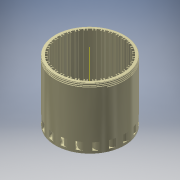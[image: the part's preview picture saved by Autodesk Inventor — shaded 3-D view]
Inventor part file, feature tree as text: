
AUTODESK INVENTOR PART (.ipt)
format: ipt  version: 2017 (Build 210142000, 142)  size: 1,598,976 bytes
history: native  units: mm
features: sketch x10, extrude x8, pattern_circular x4, fillet x2, chamfer x2, sweep x1, other x1
ambient origin geometry x8: Origin, YZ Plane, XZ Plane, XY Plane, X Axis, Y Axis, Z Axis, Center Point
bodies: Solid1 (feature_tree)
feature tree (28):
  extrude  "Extrusion1"  Depth=174.5mm
  extrude  "Extrusion2"  Depth=12.75mm
  pattern_circular  "Circular Pattern1"  Count=32 Angle=360.0deg
  extrude  "Extrusion3"  Depth=10.0mm
  pattern_circular  "Circular Pattern2"  [2 undecoded]
  extrude  "Extrusion4"  Depth=10.0mm
  extrude  "Extrusion5"  Depth=10.0mm
  pattern_circular  "Circular Pattern4"  [2 undecoded]
  extrude  "Extrusion6"  Depth=10.0mm TaperAngle=360.0deg
  fillet  "Fillet2"  Radius=35.0mm
  pattern_circular  "Circular Pattern5"  [2 undecoded]
  sweep  "Sweep2"
  extrude  "Extrusion11"  Depth=10.0mm
  chamfer  "Chamfer3"  Distance=30.0mm
  extrude  "Extrusion12"  Depth=10.0mm TaperAngle=360.0deg
  fillet  "Fillet3"  Radius=10.0mm
  chamfer  "Chamfer4"  Distance=16.0mm
  sketch  "Sketch1"  dims[d0=280.0mm d17=174.5mm]
  sketch  "Sketch2"  dims[d40=203.2mm d41=0.0mm d42=12.75mm]
  sketch  "Sketch4"  dims[d43=6.4mm]
  sketch  "Sketch5"  dims[d44=2.0mm]
  sketch  "Sketch6"  dims[d45=1.0mm]
  sketch  "Sketch7"  dims[d46=244.0mm]
  sketch  "Sketch15"  dims[d47=123.0mm]
  sketch  "3D Sketch2"
  other  "Helical Curve3"
  sketch  "Sketch16"  dims[d48=152.4mm d49=0.0mm d50=320.0mm d51=360.0deg]
  sketch  "Sketch17"  dims[d54=6.4mm d55=6.4mm d56=6.4mm d57=1.0mm d58=1.0mm d59=152.4mm d60=0.0mm d61=320.0mm d62=360.0deg d69=35.0mm d70=0.0mm d71=10.0mm d72=120.0deg d74=25.0mm d75=30.0mm d76=0.0mm d77=180.0mm d78=360.0deg d80=10.0mm d81=0.0mm d82=16.0mm d90=20.0mm d91=180.0mm d92=360.0deg d139=1.0mm d141=120.0deg d142=3.0mm d143=6.0mm d144=45.0mm d145=241.87mm d146=0.0mm d147=0.0mm d148=0.0mm d149=18.0mm d150=18.0mm d151=40.0mm d152=20.0mm d153=0.0mm d154=20.0mm d155=2.0mm d156=13.823008mm d157=50.0mm d158=16.0mm d159=0.0mm d160=10.0mm d161=3.0mm d162=2.0mm d163=13.823008mm]
note: 6 required parameter values undecoded (feature->parameter linkage not recoverable at this tier; creation-order binding heuristic only, values carry confidence <= 0.55)
